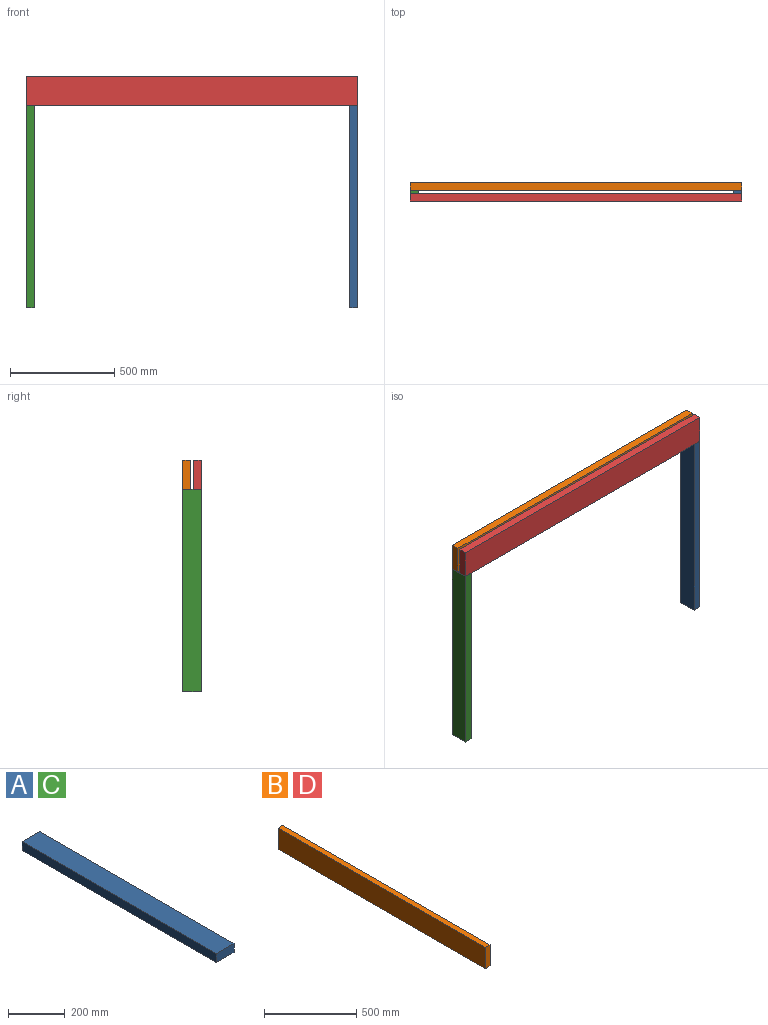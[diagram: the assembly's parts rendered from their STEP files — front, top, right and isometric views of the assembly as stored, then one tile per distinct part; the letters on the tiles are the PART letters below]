
ASSEMBLY  parts=4 mates=1
PART A: 6 faces, bbox 88.9x971.6x38.1 mm
  f0: plane 971.55x88.9mm, normal (0,0,1), area 86370.8mm2, adj f1,f3,f4,f5
  f1: plane 971.55x38.1mm, normal (-1,0,0), area 37016.1mm2, adj f0,f2,f4,f5
  f2: plane 971.55x88.9mm, normal (0,0,-1), area 86370.8mm2, adj f1,f3,f4,f5
  f3: plane 971.55x38.1mm, normal (1,0,0), area 37016.1mm2, adj f0,f2,f4,f5
  f4: plane 88.9x38.1mm, normal (0,-1,0), area 3387.1mm2, adj f0,f1,f2,f3
  f5: plane 88.9x38.1mm, normal (0,1,0), area 3387.1mm2, adj f0,f1,f2,f3
PART B: 6 faces, bbox 38.1x1587.5x139.7 mm
  f0: plane 1587.5x139.7mm, normal (-1,0,0), area 221773.7mm2, adj f1,f3,f4,f5
  f1: plane 1587.5x38.1mm, normal (0,0,-1), area 60483.8mm2, adj f0,f2,f4,f5
  f2: plane 1587.5x139.7mm, normal (1,0,0), area 221773.7mm2, adj f1,f3,f4,f5
  f3: plane 1587.5x38.1mm, normal (0,0,1), area 60483.8mm2, adj f0,f2,f4,f5
  f4: plane 139.7x38.1mm, normal (0,-1,0), area 5322.6mm2, adj f0,f1,f2,f3
  f5: plane 139.7x38.1mm, normal (0,1,0), area 5322.6mm2, adj f0,f1,f2,f3
PART C: same geometry as A
PART D: same geometry as B
PLACE A rot(axis=(-0.58,0.58,-0.58),120deg) t=(691.01,1445.9,-1353.3)mm
PLACE B rot(axis=(0,0,-1),90deg) t=(710.06,-188.34,-311.9)mm
PLACE C rot(axis=(-0.58,0.58,-0.58),120deg) t=(-858.39,1445.9,-1353.3)mm
PLACE D rot(axis=(0,0,-1),90deg) t=(710.06,-239.14,-311.9)mm fixed
MATE fastened C.f4 <-> D.f1  axis (0,0,1) through (-877.44,-442.34,-381.75)mm
